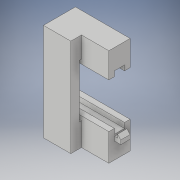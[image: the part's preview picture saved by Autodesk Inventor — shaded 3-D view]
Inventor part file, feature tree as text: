
AUTODESK INVENTOR PART (.ipt)
format: ipt  version: 2018 (Build 220112000, 112)  size: 336,384 bytes
history: native  units: in
note: dims shown in document units (in); Inventor stores cm internally (conversion verified against a paired STEP export)
features: extrude x19, sketch x18, projected_geometry x9, mirror x2, plane x1
ambient origin geometry x8: Origin, YZ Plane, XZ Plane, XY Plane, X Axis, Y Axis, Z Axis, Center Point
bodies: Solid1 (feature_tree)
feature tree (49):
  extrude  "Extrusion1"  Depth=9.0in
  extrude  "Extrusion2"  Depth=15.7in
  extrude  "Extrusion3"  Depth=0.5in
  extrude  "Extrusion4"  Depth=0.5in TaperAngle=0.0deg
  extrude  "Extrusion5"  Depth=1.05in
  extrude  "Extrusion6"  Depth=18.0in TaperAngle=0.0deg
  extrude  "Extrusion7"  Depth=3.25in
  extrude  "Extrusion11"  Depth=3.45in
  extrude  "Extrusion12"  Depth=3.25in
  plane  "Work Plane1"
  mirror  "Mirror1"
  extrude  "Extrusion14"  Depth=2.1in TaperAngle=0.0deg
  extrude  "Extrusion15"  Depth=0.75in TaperAngle=0.0deg
  extrude  "Extrusion16"  Depth=0.75in
  extrude  "Extrusion17"  Depth=0.75in
  mirror  "Mirror2"
  extrude  "Extrusion18"  Depth=4.95in
  extrude  "Extrusion19"  Depth=4.95in
  extrude  "Extrusion20"  TaperAngle=0.0deg  [1 undecoded]
  extrude  "Extrusion8"  Depth=1.5in TaperAngle=0.0deg
  extrude  "Extrusion9"  Depth=0.12in
  extrude  "Extrusion10"  Depth=0.13in
  sketch  "Sketch1"  dims[d0=16.7in d1=9.0in]
  sketch  "Sketch2"  dims[d2=6.5in d3=0.0in d4=15.7in]
  sketch  "Sketch4"  dims[d5=6.5in d6=0.5in]
  projected_geometry  "Projected Loop1"
  sketch  "Sketch5"  dims[d7=0.5in d8=5.85in d9=0.0in]
  projected_geometry  "Projected Loop2"
  sketch  "Sketch7"  dims[d10=3.775in d11=1.05in]
  projected_geometry  "Projected Loop4"
  sketch  "Sketch8"  dims[d12=2.475in d13=18.0in d14=0.0in]
  projected_geometry  "Projected Loop5"
  sketch  "Sketch9"  dims[d15=3.45in d16=3.25in]
  projected_geometry  "Projected Loop6"
  sketch  "Sketch10"  dims[d17=2.3in d18=3.45in]
  projected_geometry  "Projected Loop7"
  sketch  "Sketch11"  dims[d19=3.7in d20=3.25in]
  sketch  "Sketch12"  dims[d21=3.0in d22=0.0in d23=2.1in d24=0.0in]
  projected_geometry  "Projected Loop8"
  sketch  "Sketch13"  dims[d25=0.75in d26=0.0in d27=0.75in d28=0.0in]
  projected_geometry  "Projected Loop9"
  sketch  "Sketch15"  dims[d29=0.75in d30=0.75in]
  sketch  "Sketch17"  dims[d31=0.75in d32=0.75in]
  sketch  "Sketch18"  dims[d33=4.95in d34=4.95in]
  sketch  "Sketch19"  dims[d35=4.95in d36=4.95in]
  projected_geometry  "Projected Loop10"
  sketch  "Sketch21"  dims[d37=4.0in d38=0.0in d39=0.0in]
  sketch  "Sketch22"  dims[d40=1.5in d41=0.0in d42=1.5in d43=0.0in]
  sketch  "Sketch23"  dims[d44=0.24in d45=0.12in d46=0.13in d47=3.25in d48=0.0in d49=0.2in d50=0.0in d55=0.22in d56=0.075in d57=0.15in d58=0.0in d60=0.15in d61=0.04in d62=1.0in d63=0.0in d64=0.075in d65=0.081in d66=0.22in d67=0.0in d68=0.06in d69=0.0in d70=1.0in d71=0.0in d72=0.25in d73=0.0in d74=0.05in d75=0.1in d76=0.1in d77=1.0in d78=0.0in]
note: 1 required parameter value undecoded (feature->parameter linkage not recoverable at this tier; creation-order binding heuristic only, values carry confidence <= 0.55)
